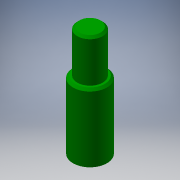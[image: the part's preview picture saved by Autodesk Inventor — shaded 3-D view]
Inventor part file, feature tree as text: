
AUTODESK INVENTOR PART (.ipt)
format: ipt  version: 2016 (Build 200138000, 138)  size: 132,608 bytes
history: native  units: in
note: dims shown in document units (in); Inventor stores cm internally (conversion verified against a paired STEP export)
features: extrude x1, other x1, sketch x1, chamfer x1
ambient origin geometry x8: Origin, YZ Plane, XZ Plane, XY Plane, X Axis, Y Axis, Z Axis, Center Point
bodies: Solid1 (feature_tree)
feature tree (4):
  extrude  "Extrusion1"  [1 undecoded]
  other  "Work Point1"
  sketch  "Sketch1"  dims[d0=0.3937in d1=0.0in]
  chamfer  "Fase2"  [1 undecoded]
note: 2 required parameter values undecoded (feature->parameter linkage not recoverable at this tier; creation-order binding heuristic only, values carry confidence <= 0.55)
